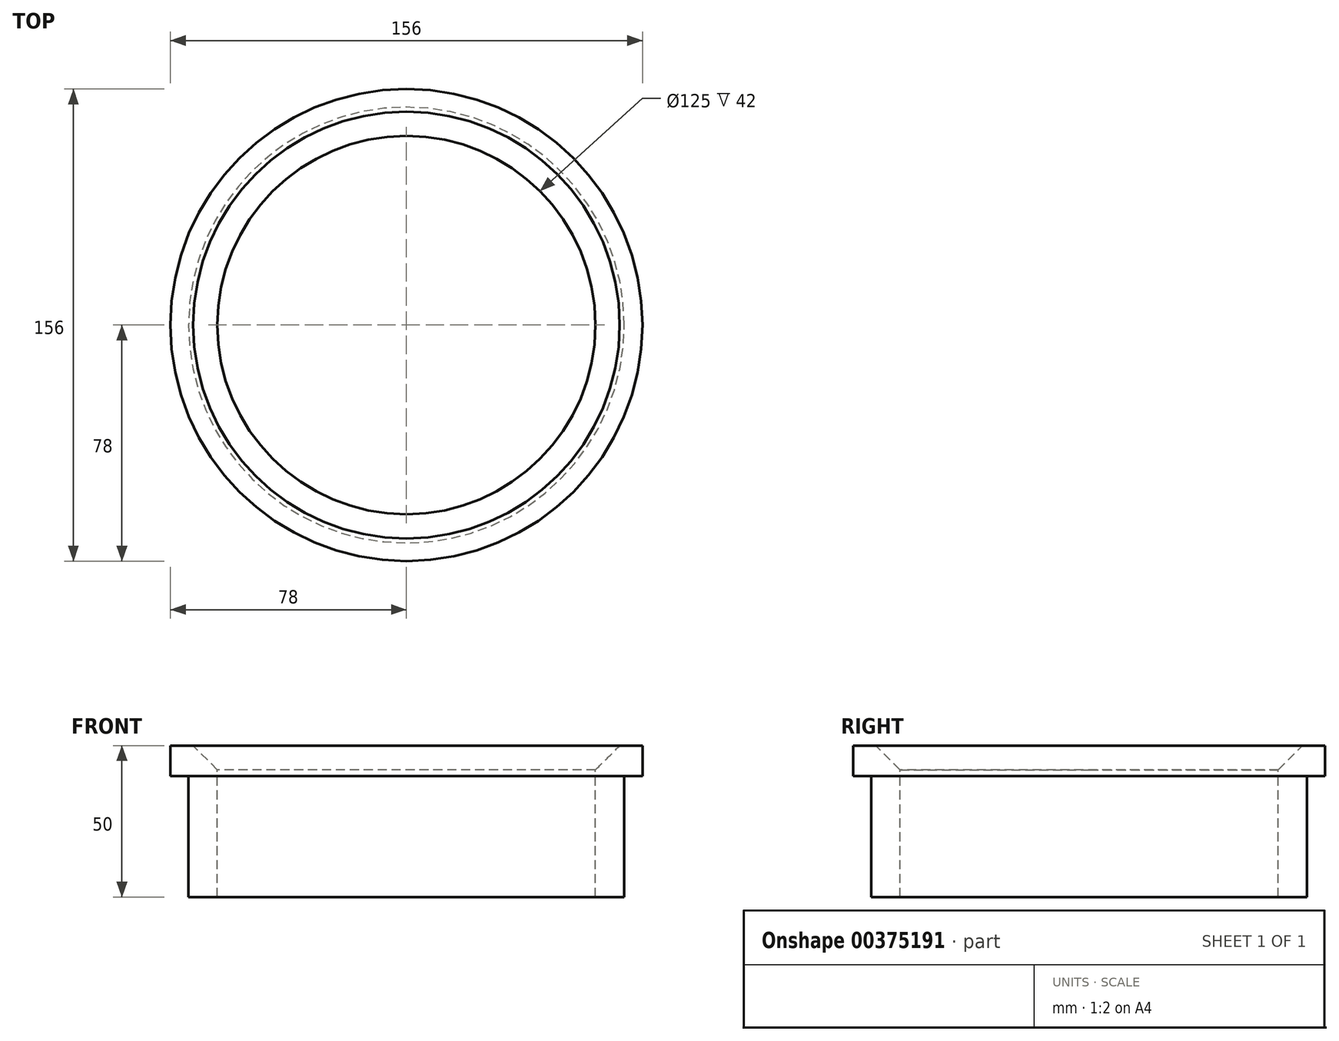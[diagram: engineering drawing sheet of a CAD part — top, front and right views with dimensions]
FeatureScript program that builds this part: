
annotation { "Feature Type Name" : "Feature", "Feature Type Description" : "" }
export const myFeature = defineFeature(function(context is Context, id is Id, definition is map)
    precondition{}
    {
        {
            var Q0;
            Q0=qCreatedBy(makeId("Top.planeOp"),FACE);
            var sketch = newSketch(context, id + "F0", { "sketchPlane" : qUnion([Q0])});
            skCircle(sketch, "E0", {"center": v(0, 0) * mm, "radius": 72 * mm});
            skSolve(sketch);
        }
        {
            var Q0;
            Q0=makeQuery(id+"F0.imprint","IMPRINT",FACE,{"disambiguationData":[TD([[makeQuery(id+"F0.imprint","IMPRINT",EDGE,{"derivedFrom":sQuery(id+"F0.wireOp",EDGE,"E0")}),1.0]])]});
            extrude(context, id + "F1", {"entities" : qUnion([Q0]), "depth" : 40 * mm});
        }
        {
            var Q0;
            Q0=makeQuery(id+"F1.opExtrude","CAP_FACE",FACE,{"disambiguationData":[OSD([sQuery(id+"F0.wireOp",EDGE,"E0")])],"isStart":false});
            var sketch = newSketch(context, id + "F2", { "sketchPlane" : qUnion([Q0])});
            skCircle(sketch, "E1", {"center": v(0, 0) * mm, "radius": 78 * mm});
            skSolve(sketch);
        }
        {
            var Q0;
            Q0 = qSketchRegion(id + "F2", true);
            extrude(context, id + "F3", {"entities" : qUnion([Q0]), "operationType" : NewBodyOperationType.ADD, "depth" : 10 * mm});
        }
        {
            var Q0;
            Q0=qCreatedBy(makeId("Front.planeOp"),FACE);
            var sketch = newSketch(context, id + "F4", { "sketchPlane" : qUnion([Q0])});
            skLineSegment(sketch, "E2", {"start": v(0, 50) * mm, "end": v(70.5, 50) * mm});
            skLineSegment(sketch, "E3", {"start": v(70.5, 50) * mm, "end": v(62.5, 42) * mm});
            skLineSegment(sketch, "E4", {"start": v(62.5, 42) * mm, "end": v(62.5, 0) * mm});
            skLineSegment(sketch, "E5", {"start": v(62.5, 0) * mm, "end": v(0, 0) * mm});
            skLineSegment(sketch, "E6", {"start": v(0, 0) * mm, "end": v(0, 50) * mm});
            skSolve(sketch);
        }
        {
            var Q0;
            Q0 = qSketchRegion(id + "F4", true);
            var Q1;
            Q1=makeQuery(id+"F3.opExtrude","CAP_EDGE",EDGE,{"disambiguationData":[OSD([sQuery(id+"F2.wireOp",EDGE,"E1")])],"isStart":false});
            revolve(context, id + "F5", {"operationType" : NewBodyOperationType.REMOVE, "entities" : qUnion([Q0]), "axis" : qUnion([Q1]), "revolveType" : RevolveType.FULL, "oppositeDirection" : true});
        }
    });
